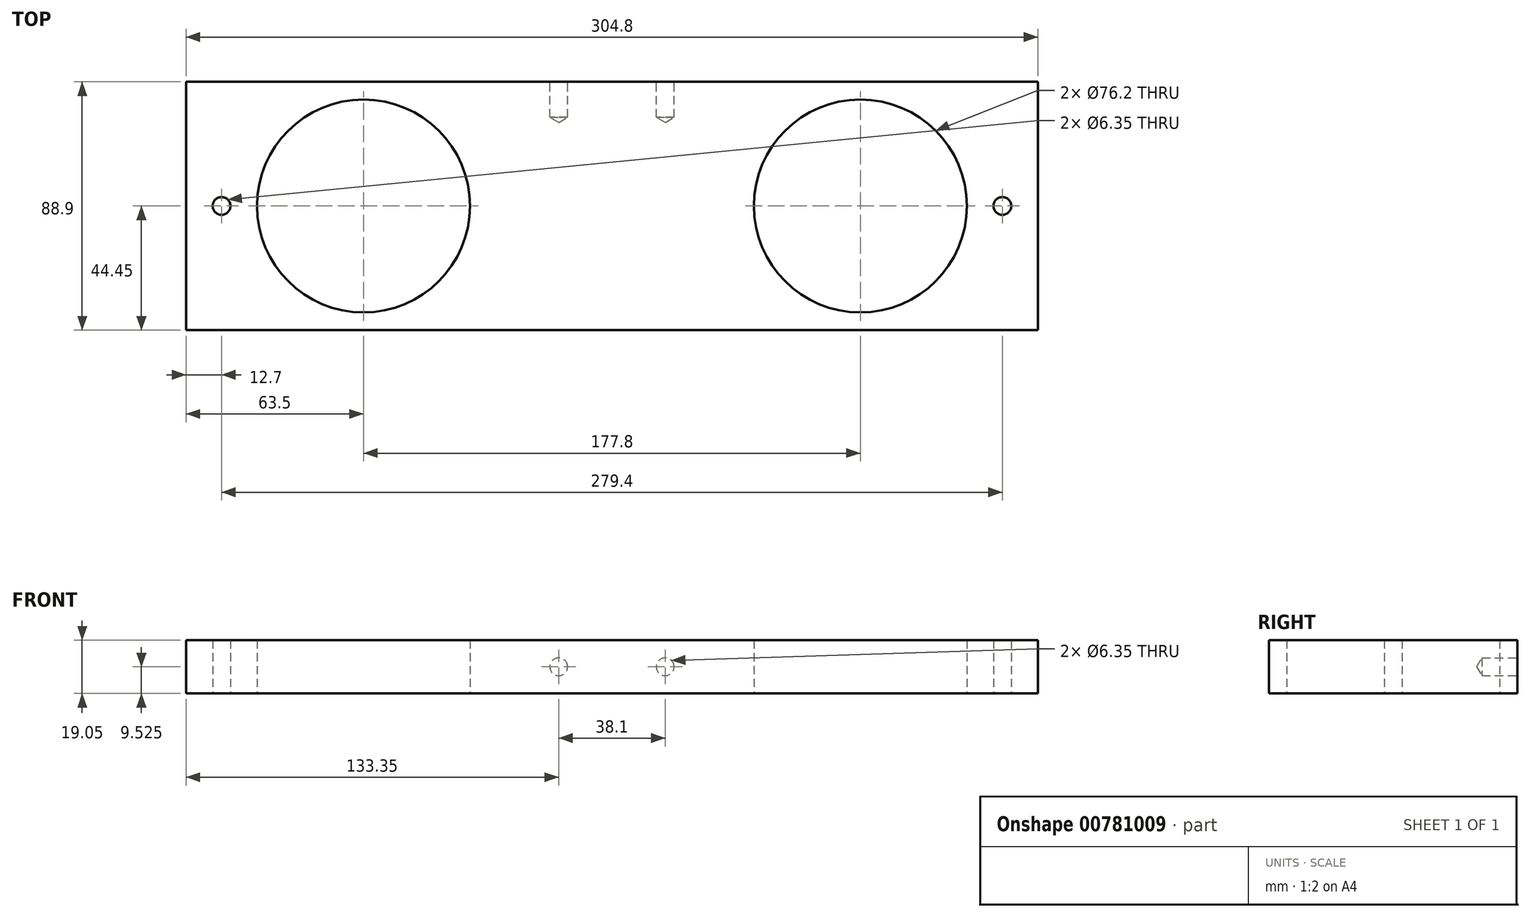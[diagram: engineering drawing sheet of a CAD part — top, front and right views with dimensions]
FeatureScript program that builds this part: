
annotation { "Feature Type Name" : "Feature", "Feature Type Description" : "" }
export const myFeature = defineFeature(function(context is Context, id is Id, definition is map)
    precondition{}
    {
        {
            var Q0;
            Q0=qCreatedBy(makeId("Top.planeOp"),FACE);
            var sketch = newSketch(context, id + "F0", { "sketchPlane" : qUnion([Q0])});
            skLineSegment(sketch, "E0.bottom", {"start": v(-152.4, 88.9) * mm, "end": v(0, 88.9) * mm});
            skLineSegment(sketch, "E0.top", {"start": v(-152.4, 0) * mm, "end": v(0, 0) * mm});
            skLineSegment(sketch, "E0.left", {"start": v(-152.4, 88.9) * mm, "end": v(-152.4, 0) * mm});
            skLineSegment(sketch, "E0.right", {"start": v(0, 88.9) * mm, "end": v(0, 0) * mm});
            skCircle(sketch, "E1", {"center": v(-63.5, 44.45) * mm, "radius": 38.1 * mm});
            skLineSegment(sketch, "E2", {"start": v(0, 44.45) * mm, "end": v(-152.4, 44.45) * mm, "construction": true});
            skSolve(sketch);
        }
        {
            var Q0;
            Q0=makeQuery(id+"F0.imprint","IMPRINT",FACE,{"disambiguationData":[TD([[makeQuery(id+"F0.imprint","IMPRINT",EDGE,{"derivedFrom":sQuery(id+"F0.wireOp",EDGE,"E0.bottom")}),-1.0]])]});
            extrude(context, id + "F1", {"entities" : qUnion([Q0]), "depth" : 19.05 * mm, "offsetDistance" : 25.4 * mm});
        }
        {
            var Q0;
            Q0=makeQuery(id+"F1.opExtrude","SWEPT_BODY",BODY,{"disambiguationData":[OSD([sQuery(id+"F0.wireOp",EDGE,"E0.bottom"),sQuery(id+"F0.wireOp",EDGE,"E0.top"),sQuery(id+"F0.wireOp",EDGE,"E0.left"),sQuery(id+"F0.wireOp",EDGE,"E0.right"),sQuery(id+"F0.wireOp",EDGE,"E1")])]});
            var Q1;
            Q1=makeQuery(id+"F1.opExtrude","SWEPT_FACE",FACE,{"disambiguationData":[OSD([sQuery(id+"F0.wireOp",EDGE,"E0.left")])]});
            mirror(context, id + "F2", {"operationType" : NewBodyOperationType.ADD, "entities" : qUnion([Q0]), "mirrorPlane" : qUnion([Q1])});
        }
        {
            var Q0;
            {var subQ0=makeQuery(id+"F1.opExtrude","SWEPT_FACE",FACE,{"disambiguationData":[OSD([sQuery(id+"F0.wireOp",EDGE,"E0.bottom")])]});Q0=makeQuery(id+"F2.boolean.opBoolean","MERGE",FACE,{"derivedFrom":[subQ0,makeQuery(id+"F2.opPattern","COPY",FACE,{"derivedFrom":subQ0,"instanceName":"1"})]});}
            var sketch = newSketch(context, id + "F3", { "sketchPlane" : qUnion([Q0])});
            skPoint(sketch, "E3", {"position": v(133.35, 9.53) * mm});
            skLineSegment(sketch, "E4", {"start": v(133.35, 19.05) * mm, "end": v(133.35, 0) * mm, "construction": true});
            skLineSegment(sketch, "E5", {"start": v(171.45, 19.05) * mm, "end": v(171.45, 0) * mm, "construction": true});
            skLineSegment(sketch, "E6", {"start": v(171.45, 9.53) * mm, "end": v(133.35, 9.53) * mm, "construction": true});
            skPoint(sketch, "E7", {"position": v(171.45, 9.53) * mm});
            skSolve(sketch);
        }
        {
            var Q0;
            Q0=sQuery(id+"F3.wireOp",VERTEX,"E3");
            var Q1;
            Q1=sQuery(id+"F3.wireOp",VERTEX,"E7");
            var Q2;
            Q2=makeQuery(id+"F1.opExtrude","SWEPT_BODY",BODY,{"disambiguationData":[OSD([sQuery(id+"F0.wireOp",EDGE,"E0.bottom"),sQuery(id+"F0.wireOp",EDGE,"E0.top"),sQuery(id+"F0.wireOp",EDGE,"E0.left"),sQuery(id+"F0.wireOp",EDGE,"E0.right"),sQuery(id+"F0.wireOp",EDGE,"E1")])]});
            hole(context, id + "F4", {"style" : HoleStyle.SIMPLE, "endStyle" : HoleEndStyle.BLIND, "holeDiameter" : 6.35 * mm, "majorDiameter" : 6.35 * mm, "holeDepth" : 12.7 * mm, "isTappedThrough" : true, "tappedDepth" : 12.7 * mm, "tapClearance" : 3, "locations" : qUnion([Q0, Q1]), "scope" : qUnion([Q2])});
        }
        {
            var Q0;
            {var subQ0=makeQuery(id+"F1.opExtrude","CAP_FACE",FACE,{"disambiguationData":[OSD([sQuery(id+"F0.wireOp",EDGE,"E0.bottom"),sQuery(id+"F0.wireOp",EDGE,"E0.top"),sQuery(id+"F0.wireOp",EDGE,"E0.left"),sQuery(id+"F0.wireOp",EDGE,"E0.right"),sQuery(id+"F0.wireOp",EDGE,"E1")])],"isStart":true});Q0=makeQuery(id+"F2.boolean.opBoolean","MERGE",FACE,{"derivedFrom":[subQ0,makeQuery(id+"F2.opPattern","COPY",FACE,{"derivedFrom":subQ0,"instanceName":"1"})]});}
            var sketch = newSketch(context, id + "F5", { "sketchPlane" : qUnion([Q0])});
            skLineSegment(sketch, "E8", {"start": v(-304.8, -44.45) * mm, "end": v(-292.1, -44.45) * mm, "construction": true});
            skLineSegment(sketch, "E9.MirrorCS", {"start": v(0, -44.45) * mm, "end": v(-12.7, -44.45) * mm, "construction": true});
            skSolve(sketch);
        }
        {
            var Q0;
            Q0=sQuery(id+"F5.wireOp",VERTEX,"E8.end");
            var Q1;
            Q1=sQuery(id+"F5.wireOp",VERTEX,"E9.MirrorCS.end");
            var Q2;
            Q2=makeQuery(id+"F1.opExtrude","SWEPT_BODY",BODY,{"disambiguationData":[OSD([sQuery(id+"F0.wireOp",EDGE,"E0.bottom"),sQuery(id+"F0.wireOp",EDGE,"E0.top"),sQuery(id+"F0.wireOp",EDGE,"E0.left"),sQuery(id+"F0.wireOp",EDGE,"E0.right"),sQuery(id+"F0.wireOp",EDGE,"E1")])]});
            hole(context, id + "F6", {"style" : HoleStyle.SIMPLE, "endStyle" : HoleEndStyle.THROUGH, "holeDiameter" : 6.35 * mm, "majorDiameter" : 6.35 * mm, "isTappedThrough" : true, "tappedDepth" : 12.7 * mm, "tapClearance" : 3, "locations" : qUnion([Q0, Q1]), "scope" : qUnion([Q2])});
        }
    });
